# Revit family: ALUMINI
name_source: partatom
category: Connessioni strutturali
revit_build: Autodesk Revit 2016 (Build: 20151007_0715(x64)
units: mm (PartAtom-declared; Revit-internal decimal feet)

## family parameters
Attiva taglio nelle viste = No
Condiviso = No
Host = Superficie
Materiale per comportamento modello = Altro
Numero OmniClass = 23.20.40.11.24.14
Taglio con vuoti quando caricato = Sì
Titolo OmniClass = Wood Connectors

## types (5) — shared parameters
Catalogo = Piastre e connettori per legno
Family Version = 1.0.0
Fori diametro = 7 mm  [stored 0.0229659 ft]
Larghezza ala = 45 mm  [stored 0.147638 ft]
Lunghezza anima = 109.9 mm  [stored 0.360564 ft]
Materiale = <Per categoria>
Produttore = Rotho Blaas srl
Spessore = 6 mm  [stored 0.019685 ft]
URL = http://www.rothoblaas.com
zero-valued in all types: Prospetto di default

## per-type parameters (varying)
| type | Altezza |
| ALUMINI   65 | 65 mm  [stored 0.213255 ft] |
| ALUMINI   95 | 95 mm |
| ALUMINI 125 | 125 mm |
| ALUMINI 185 | 185 mm |
| ALUMINI 155 | 155 mm |

note: [stored X ft] marks values corroborated as IEEE doubles in the binary element streams (Revit-internal decimal feet)
